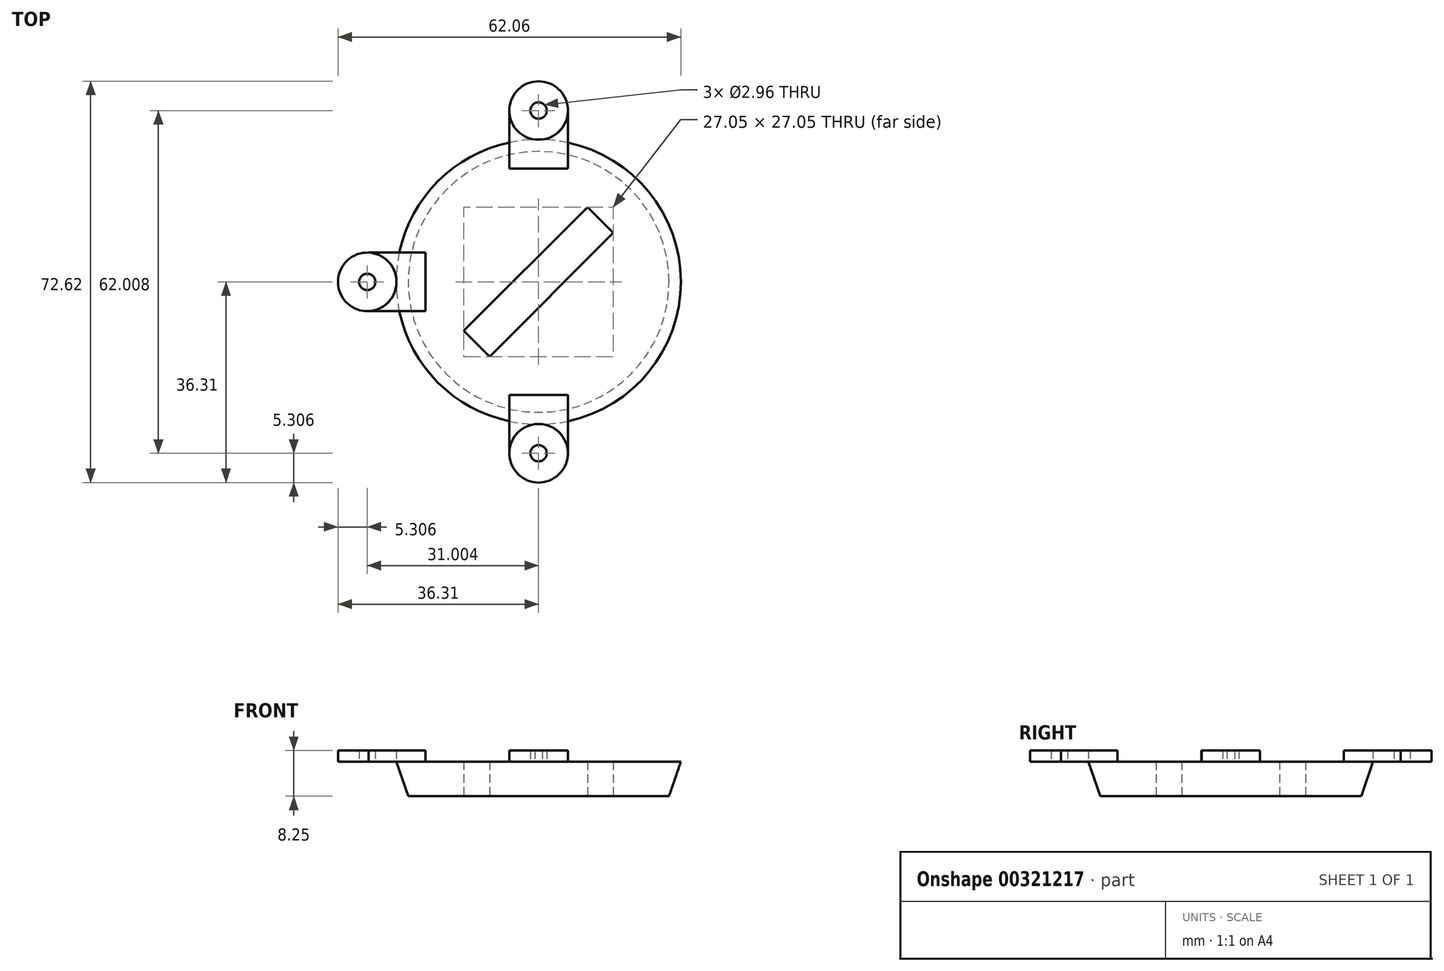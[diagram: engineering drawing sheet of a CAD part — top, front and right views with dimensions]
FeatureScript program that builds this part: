
annotation { "Feature Type Name" : "Feature", "Feature Type Description" : "" }
export const myFeature = defineFeature(function(context is Context, id is Id, definition is map)
    precondition{}
    {
        {
            var Q0;
            Q0=qCreatedBy(makeId("Top.planeOp"),FACE);
            var sketch = newSketch(context, id + "F0", { "sketchPlane" : qUnion([Q0])});
            skCircle(sketch, "E0", {"center": v(0, 0) * mm, "radius": 23.6 * mm});
            skSolve(sketch);
        }
        {
            var Q0;
            Q0=qCreatedBy(makeId("Top.planeOp"),FACE);
            cPlane(context, id + "F1", {"entities" : qUnion([Q0]), "cplaneType" : CPlaneType.OFFSET, "offset" : 6.25 * mm, "width" : 150 * mm, "height" : 150 * mm});
        }
        {
            var Q0;
            Q0=qCreatedBy(id+"F1.planeOp",FACE);
            var sketch = newSketch(context, id + "F2", { "sketchPlane" : qUnion([Q0])});
            skCircle(sketch, "E1", {"center": v(0, 0) * mm, "radius": 25.75 * mm});
            skSolve(sketch);
        }
        {
            var Q0;
            Q0=makeQuery(id+"F2.imprint","IMPRINT",FACE,{"disambiguationData":[TD([[makeQuery(id+"F2.imprint","IMPRINT",EDGE,{"derivedFrom":sQuery(id+"F2.wireOp",EDGE,"E1")}),1.0]])]});
            var Q1;
            Q1=makeQuery(id+"F0.imprint","IMPRINT",FACE,{"disambiguationData":[TD([[makeQuery(id+"F0.imprint","IMPRINT",EDGE,{"derivedFrom":sQuery(id+"F0.wireOp",EDGE,"E0")}),1.0]])]});
            loft(context, id + "F3", {"sheetProfilesArray" : [{ "sheetProfileEntities" : qUnion([Q0]) }, { "sheetProfileEntities" : qUnion([Q1]) }]});
        }
        {
            var Q0;
            Q0=makeQuery(id+"F3.opLoft","CAP_FACE",FACE,{"disambiguationData":[OSD([makeQuery(id+"F2.imprint","IMPRINT",FACE,{"disambiguationData":[TD([[makeQuery(id+"F2.imprint","IMPRINT",EDGE,{"derivedFrom":sQuery(id+"F2.wireOp",EDGE,"E1")}),1.0]])]})])],"isStart":true});
            var sketch = newSketch(context, id + "F4", { "sketchPlane" : qUnion([Q0])});
            skLineSegment(sketch, "E2", {"start": v(0, 25.75) * mm, "end": v(0, 36.25) * mm});
            skCircle(sketch, "E3", {"center": v(0, 31) * mm, "radius": 5.3 * mm});
            skCircle(sketch, "E4", {"center": v(0, 31) * mm, "radius": 1.48 * mm});
            skSolve(sketch);
        }
        {
            var Q0;
            {var subQ1=makeQuery(id+"F3.opLoft","MID_CAP_EDGE",EDGE,{"disambiguationData":[OSD([sQuery(id+"F2.wireOp",EDGE,"E1")])],"capPos":0.0});var subQ4=makeQuery(id+"F4.imprint","IMPRINT",VERTEX,{"derivedFrom":subQ1});Q0=makeQuery(id+"F4.imprint","IMPRINT",FACE,{"disambiguationData":[TD([[makeQuery(id+"F4.imprint","IMPRINT",EDGE,{"disambiguationData":[TD([[subQ4,1.0]])],"derivedFrom":subQ1}),1.0]])]});}
            var sketch = newSketch(context, id + "F5", { "sketchPlane" : qUnion([Q0])});
            skLineSegment(sketch, "E5.bottom", {"start": v(-5.3, 20.48) * mm, "end": v(5.3, 20.48) * mm});
            skLineSegment(sketch, "E5.top", {"start": v(-5.3, 31.08) * mm, "end": v(5.3, 31.08) * mm});
            skLineSegment(sketch, "E5.left", {"start": v(-5.3, 20.48) * mm, "end": v(-5.3, 31.08) * mm});
            skLineSegment(sketch, "E5.right", {"start": v(5.3, 20.48) * mm, "end": v(5.3, 31.08) * mm});
            skPoint(sketch, "E5.middle", {"position": v(0, 25.78) * mm});
            skSolve(sketch);
        }
        {
            var Q0;
            {var subQ0=makeQuery(id+"F3.opLoft","MID_CAP_EDGE",EDGE,{"disambiguationData":[OSD([sQuery(id+"F2.wireOp",EDGE,"E1")])],"capPos":0.0});var subQ1=makeQuery(id+"F4.imprint","IMPRINT",VERTEX,{"derivedFrom":subQ0});Q0=makeQuery(id+"F4.imprint","IMPRINT",FACE,{"disambiguationData":[TD([[makeQuery(id+"F4.imprint","IMPRINT",EDGE,{"disambiguationData":[TD([[subQ1,1.0]])],"derivedFrom":subQ0}),1.0]])]});}
            var Q1;
            {var subQ6=sQuery(id+"F5.wireOp",EDGE,"E5.bottom");Q1=makeQuery(id+"F5.imprint","IMPRINT",FACE,{"disambiguationData":[TD([[makeQuery(id+"F5.imprint","IMPRINT",EDGE,{"derivedFrom":subQ6}),1.0]])]});}
            extrude(context, id + "F6", {"entities" : qUnion([Q0, Q1]), "depth" : 2 * mm});
        }
        {
            var Q0;
            Q0=qCreatedBy(makeId("Front.planeOp"),FACE);
            var sketch = newSketch(context, id + "F7", { "sketchPlane" : qUnion([Q0])});
            skLineSegment(sketch, "E6", {"start": v(0, 0) * mm, "end": v(0, 41.82) * mm});
            skSolve(sketch);
        }
        {
            var Q0;
            Q0=makeQuery(id+"F6.opExtrude","SWEPT_BODY",BODY,{"disambiguationData":[OSD([sQuery(id+"F2.wireOp",EDGE,"E1"),sQuery(id+"F4.wireOp",EDGE,"E3")])]});
            var Q1;
            Q1=makeQuery(id+"F6.opExtrude","SWEPT_BODY",BODY,{"disambiguationData":[OSD([sQuery(id+"F5.wireOp",EDGE,"E5.bottom"),sQuery(id+"F5.wireOp",EDGE,"E5.top"),sQuery(id+"F5.wireOp",EDGE,"E5.left"),sQuery(id+"F5.wireOp",EDGE,"E5.right")])]});
            var Q2;
            Q2=sQuery(id+"F7.wireOp",EDGE,"E6");
            circularPattern(context, id + "F8", {"entities" : qUnion([Q0, Q1]), "axis" : qUnion([Q2]), "angle" : 180 * degree, "instanceCount" : 3, "equalSpace" : true});
        }
        {
            var Q0;
            Q0=makeQuery(id+"F3.opLoft","CAP_FACE",FACE,{"disambiguationData":[OSD([makeQuery(id+"F2.imprint","IMPRINT",FACE,{"disambiguationData":[TD([[makeQuery(id+"F2.imprint","IMPRINT",EDGE,{"derivedFrom":sQuery(id+"F2.wireOp",EDGE,"E1")}),1.0]])]})])],"isStart":true});
            var sketch = newSketch(context, id + "F9", { "sketchPlane" : qUnion([Q0])});
            skLineSegment(sketch, "E7.bottom", {"start": v(15.83, 3.3) * mm, "end": v(-15.83, 3.3) * mm});
            skLineSegment(sketch, "E7.top", {"start": v(15.83, -3.3) * mm, "end": v(-15.83, -3.3) * mm});
            skLineSegment(sketch, "E7.left", {"start": v(15.83, 3.3) * mm, "end": v(15.83, -3.3) * mm});
            skLineSegment(sketch, "E7.right", {"start": v(-15.83, 3.3) * mm, "end": v(-15.83, -3.3) * mm});
            skPoint(sketch, "E7.middle", {"position": v(0, 0) * mm});
            skSolve(sketch);
        }
        {
            var Q0;
            Q0=makeQuery(id+"F9.imprint","IMPRINT",FACE,{"disambiguationData":[TD([[makeQuery(id+"F9.imprint","IMPRINT",EDGE,{"derivedFrom":sQuery(id+"F9.wireOp",EDGE,"E7.bottom")}),1.0]])]});
            extrude(context, id + "F10", {"entities" : qUnion([Q0]), "endBound" : BoundingType.SYMMETRIC, "depth" : 25 * mm});
        }
        {
            var Q0;
            Q0=makeQuery(id+"F10.opExtrude","SWEPT_BODY",BODY,{"disambiguationData":[OSD([sQuery(id+"F9.wireOp",EDGE,"E7.bottom"),sQuery(id+"F9.wireOp",EDGE,"E7.top"),sQuery(id+"F9.wireOp",EDGE,"E7.left"),sQuery(id+"F9.wireOp",EDGE,"E7.right")])]});
            var Q1;
            Q1=qCreatedBy(makeId("Origin.pointOp"),VERTEX);
            var Q2;
            Q2=sQuery(id+"F7.wireOp",EDGE,"E6");
            transform(context, id + "F11", {"entities" : qUnion([Q0]), "transformType" : TransformType.ROTATION, "transformAxis" : qUnion([Q2]), "angle" : 45 * degree, "makeCopy" : false});
        }
        {
            var Q0;
            Q0=makeQuery(id+"F10.opExtrude","SWEPT_BODY",BODY,{"disambiguationData":[OSD([sQuery(id+"F9.wireOp",EDGE,"E7.bottom"),sQuery(id+"F9.wireOp",EDGE,"E7.top"),sQuery(id+"F9.wireOp",EDGE,"E7.left"),sQuery(id+"F9.wireOp",EDGE,"E7.right")])]});
            var Q1;
            Q1=makeQuery(id+"F3.opLoft","SWEPT_BODY",BODY,{"disambiguationData":[OSD([makeQuery(id+"F0.imprint","IMPRINT",FACE,{"disambiguationData":[TD([[makeQuery(id+"F0.imprint","IMPRINT",EDGE,{"derivedFrom":sQuery(id+"F0.wireOp",EDGE,"E0")}),1.0]])]}),makeQuery(id+"F2.imprint","IMPRINT",FACE,{"disambiguationData":[TD([[makeQuery(id+"F2.imprint","IMPRINT",EDGE,{"derivedFrom":sQuery(id+"F2.wireOp",EDGE,"E1")}),1.0]])]})])]});
            booleanBodies(context, id + "F12", {"operationType" : BooleanOperationType.SUBTRACTION, "tools" : qUnion([Q0]), "targets" : qUnion([Q1])});
        }
    });
